# Revit family: Sanitary_Taps-Mixers_hansgrohe_Vivenis-Single-lever-basin-mixer-250-__1
name_source: partatom
category: Plumbing Fixtures
revit_build: Autodesk Revit 2018 (Build: 20170223_1515(x64)
units: mm (PartAtom-declared; Revit-internal decimal feet)

## family parameters
Always vertical = No
Cut with Voids When Loaded = No
OmniClass Number = 23.31.11.00
OmniClass Title = Faucets
Part Type = Normal
Room Calculation Point = No
Round Connector Dimension = Use Diameter
Shared = No
Work Plane-Based = Yes

## types (5) — shared parameters
Connector Description = Water Inlet 12.7 mm
Date Updated = 2023/11/24
Default Elevation = 1219.2 mm
Description = Vivenis Single lever basin mixer 250 for washbowls with waste set
Diameter = 12.7 mm  [stored 0.0416667 ft]
Edition number = 1
Manufacturer = Hansgrohe
Model = 75043CHN
Product data url = https://bimobject.com
Product url = https://www.hansgrohe.com.cn
URL = https://www.hansgrohe.com

## per-type parameters (varying)
| type | Material 1 | Version |
| 007 Chrome | Hansgrohe - Metal - 007 Chrome | 2 |
| 147 Brushed Bronze | Hansgrohe - Metal - 147 Brushed Bronze | 0 |
| 677 Matt Black | Hansgrohe - Metal - 677 Matte Black | 0 |
| 707 Matt White | Hansgrohe - Metal - 707 Matte White | 0 |
| 997 Polished Gold Optic | Hansgrohe - Metal - 997 Polished Gold Optic | 0 |

note: [stored X ft] marks values corroborated as IEEE doubles in the binary element streams (Revit-internal decimal feet)
